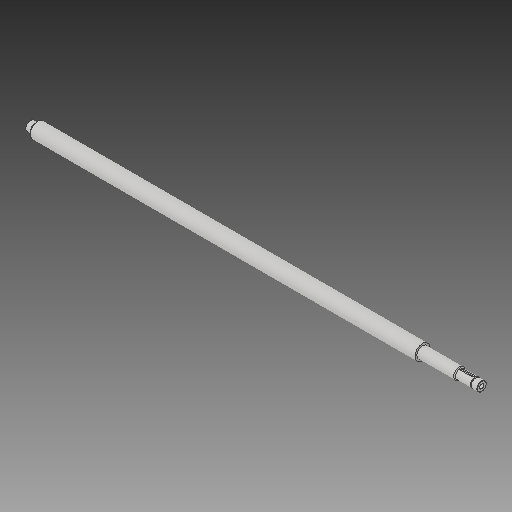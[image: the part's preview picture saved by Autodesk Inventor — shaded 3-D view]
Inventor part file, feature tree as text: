
AUTODESK INVENTOR PART (.ipt)
format: ipt  version: 2018 (Build 220112000, 112)  size: 101,888 bytes
history: native  units: in
note: dims shown in document units (in); Inventor stores cm internally (conversion verified against a paired STEP export)
features: chamfer x1
ambient origin geometry x8: Origin, YZ Plane, XZ Plane, XY Plane, X Axis, Y Axis, Z Axis, Center Point
bodies: Solid1 (feature_tree)
feature tree (1):
  chamfer  "Chamfer3"  [1 undecoded]
note: 1 required parameter value undecoded (feature->parameter linkage not recoverable at this tier; creation-order binding heuristic only, values carry confidence <= 0.55)
